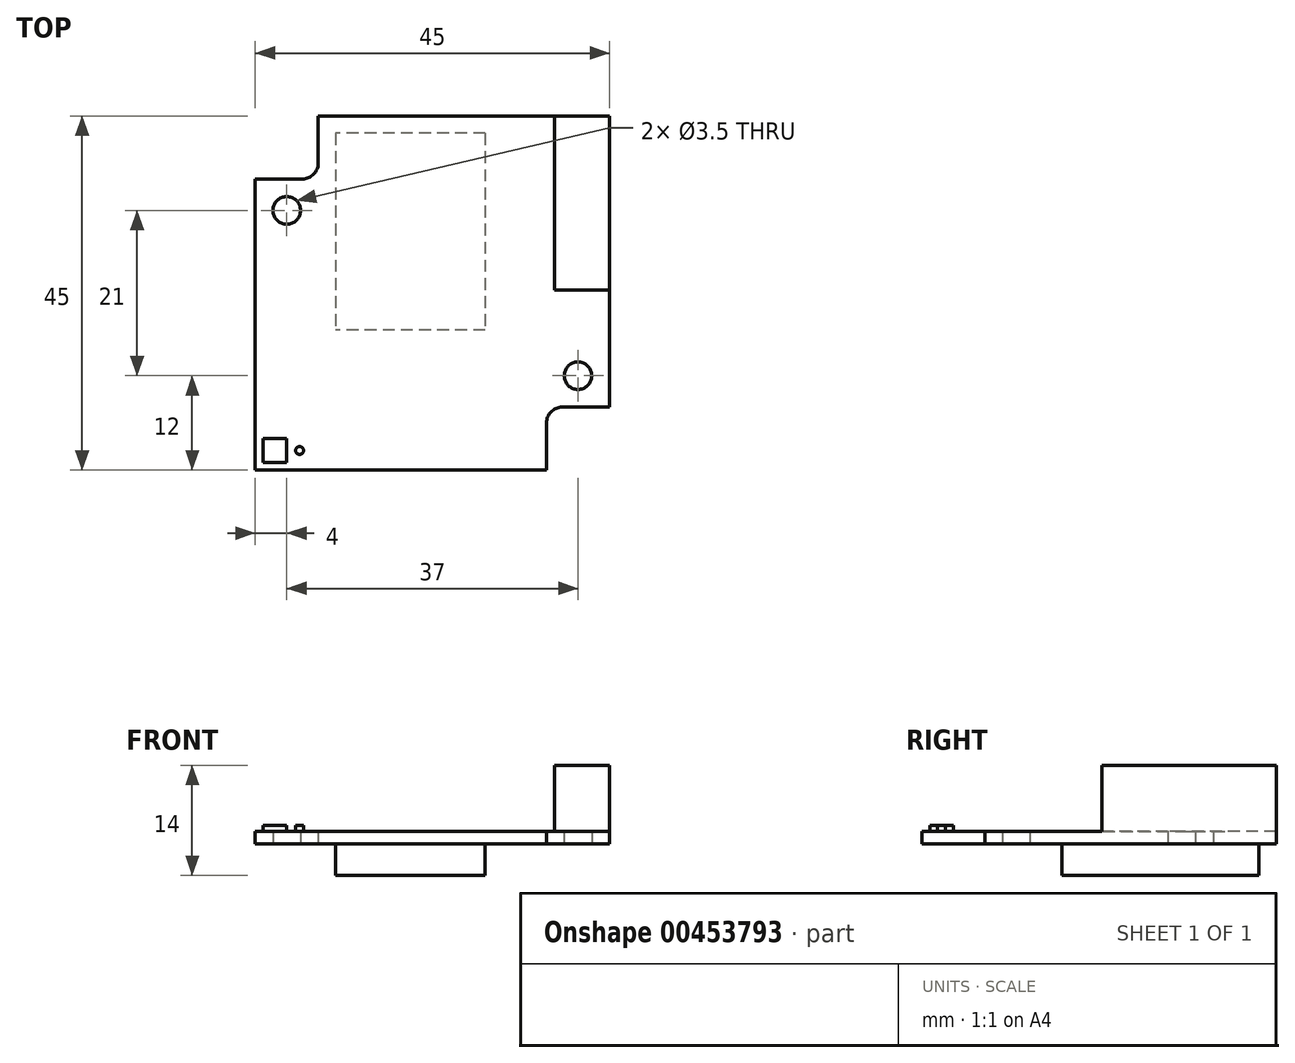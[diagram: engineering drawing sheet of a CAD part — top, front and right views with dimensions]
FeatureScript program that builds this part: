
annotation { "Feature Type Name" : "Feature", "Feature Type Description" : "" }
export const myFeature = defineFeature(function(context is Context, id is Id, definition is map)
    precondition{}
    {
        {
            var Q0;
            Q0=qCreatedBy(makeId("Top.planeOp"),FACE);
            var sketch = newSketch(context, id + "F0", { "sketchPlane" : qUnion([Q0])});
            skLineSegment(sketch, "E0.bottom", {"start": v(14.5, -22.5) * mm, "end": v(-22.5, -22.5) * mm});
            skLineSegment(sketch, "E0.top", {"start": v(22.5, 22.5) * mm, "end": v(-14.5, 22.5) * mm});
            skLineSegment(sketch, "E0.left", {"start": v(22.5, -14.5) * mm, "end": v(22.5, 22.5) * mm});
            skLineSegment(sketch, "E0.right", {"start": v(-22.5, -22.5) * mm, "end": v(-22.5, 14.5) * mm});
            skPoint(sketch, "E0.middle", {"position": v(0, 0) * mm});
            skLineSegment(sketch, "E1.top", {"start": v(-22.5, 14.5) * mm, "end": v(-16.5, 14.5) * mm});
            skLineSegment(sketch, "E1.right", {"start": v(-14.5, 22.5) * mm, "end": v(-14.5, 16.5) * mm});
            skLineSegment(sketch, "E2.top", {"start": v(22.5, -14.5) * mm, "end": v(16.5, -14.5) * mm});
            skLineSegment(sketch, "E2.right", {"start": v(14.5, -22.5) * mm, "end": v(14.5, -16.5) * mm});
            skPoint(sketch, "E3.orphan", {"position": v(-22.5, 22.5) * mm});
            skPoint(sketch, "E4.orphan", {"position": v(22.5, -22.5) * mm});
            skPoint(sketch, "E5.visualSharp", {"position": v(-14.5, 14.5) * mm});
            skArc(sketch, "E5.filletArc", {"start": v(-16.5, 14.5) * mm, "mid": v(-15.09, 15.09) * mm, "end": v(-14.5, 16.5) * mm});
            skPoint(sketch, "E6.visualSharp", {"position": v(14.5, -14.5) * mm});
            skArc(sketch, "E6.filletArc", {"start": v(16.5, -14.5) * mm, "mid": v(15.09, -15.09) * mm, "end": v(14.5, -16.5) * mm});
            skSolve(sketch);
        }
        {
            var Q0;
            Q0 = qSketchRegion(id + "F0", true);
            extrude(context, id + "F1", {"entities" : qUnion([Q0]), "depth" : 1.6 * mm});
        }
        {
            var Q0;
            Q0=makeQuery(id+"F1.opExtrude","CAP_FACE",FACE,{"disambiguationData":[OSD([sQuery(id+"F0.wireOp",EDGE,"E0.bottom"),sQuery(id+"F0.wireOp",EDGE,"E0.top"),sQuery(id+"F0.wireOp",EDGE,"E0.left"),sQuery(id+"F0.wireOp",EDGE,"E0.right"),sQuery(id+"F0.wireOp",EDGE,"E1.top"),sQuery(id+"F0.wireOp",EDGE,"E1.right"),sQuery(id+"F0.wireOp",EDGE,"E2.top"),sQuery(id+"F0.wireOp",EDGE,"E2.right"),sQuery(id+"F0.wireOp",EDGE,"E5.filletArc"),sQuery(id+"F0.wireOp",EDGE,"E6.filletArc")])],"isStart":false});
            var sketch = newSketch(context, id + "F2", { "sketchPlane" : qUnion([Q0])});
            skLineSegment(sketch, "E7.bottom", {"start": v(6.71, 20.3) * mm, "end": v(-12.29, 20.3) * mm});
            skLineSegment(sketch, "E7.top", {"start": v(6.71, -4.7) * mm, "end": v(-12.29, -4.7) * mm});
            skLineSegment(sketch, "E7.left", {"start": v(6.71, 20.3) * mm, "end": v(6.71, -4.7) * mm});
            skLineSegment(sketch, "E7.right", {"start": v(-12.29, 20.3) * mm, "end": v(-12.29, -4.7) * mm});
            skSolve(sketch);
        }
        {
            var Q0;
            Q0 = qSketchRegion(id + "F2", true);
            extrude(context, id + "F3", {"entities" : qUnion([Q0]), "operationType" : NewBodyOperationType.ADD, "depth" : -5.6 * mm});
        }
        {
            var Q0;
            Q0=makeQuery(id+"F1.opExtrude","CAP_FACE",FACE,{"disambiguationData":[OSD([sQuery(id+"F0.wireOp",EDGE,"E0.bottom"),sQuery(id+"F0.wireOp",EDGE,"E0.top"),sQuery(id+"F0.wireOp",EDGE,"E0.left"),sQuery(id+"F0.wireOp",EDGE,"E0.right"),sQuery(id+"F0.wireOp",EDGE,"E1.top"),sQuery(id+"F0.wireOp",EDGE,"E1.right"),sQuery(id+"F0.wireOp",EDGE,"E2.top"),sQuery(id+"F0.wireOp",EDGE,"E2.right"),sQuery(id+"F0.wireOp",EDGE,"E5.filletArc"),sQuery(id+"F0.wireOp",EDGE,"E6.filletArc")])],"isStart":false});
            var sketch = newSketch(context, id + "F4", { "sketchPlane" : qUnion([Q0])});
            skLineSegment(sketch, "E8.bottom", {"start": v(15.5, 22.5) * mm, "end": v(22.5, 22.5) * mm});
            skLineSegment(sketch, "E8.top", {"start": v(15.5, 0.4) * mm, "end": v(22.5, 0.4) * mm});
            skLineSegment(sketch, "E8.left", {"start": v(15.5, 22.5) * mm, "end": v(15.5, 0.4) * mm});
            skLineSegment(sketch, "E8.right", {"start": v(22.5, 22.5) * mm, "end": v(22.5, 0.4) * mm});
            skSolve(sketch);
        }
        {
            var Q0;
            Q0 = qSketchRegion(id + "F4", true);
            extrude(context, id + "F5", {"entities" : qUnion([Q0]), "operationType" : NewBodyOperationType.ADD, "depth" : 8.4 * mm});
        }
        {
            var Q0;
            Q0=makeQuery(id+"F1.opExtrude","CAP_FACE",FACE,{"disambiguationData":[OSD([sQuery(id+"F0.wireOp",EDGE,"E0.bottom"),sQuery(id+"F0.wireOp",EDGE,"E0.top"),sQuery(id+"F0.wireOp",EDGE,"E0.left"),sQuery(id+"F0.wireOp",EDGE,"E0.right"),sQuery(id+"F0.wireOp",EDGE,"E1.top"),sQuery(id+"F0.wireOp",EDGE,"E1.right"),sQuery(id+"F0.wireOp",EDGE,"E2.top"),sQuery(id+"F0.wireOp",EDGE,"E2.right"),sQuery(id+"F0.wireOp",EDGE,"E5.filletArc"),sQuery(id+"F0.wireOp",EDGE,"E6.filletArc")])],"isStart":false});
            var sketch = newSketch(context, id + "F6", { "sketchPlane" : qUnion([Q0])});
            skLineSegment(sketch, "E9.bottom", {"start": v(-21.5, -18.5) * mm, "end": v(-18.5, -18.5) * mm});
            skLineSegment(sketch, "E9.top", {"start": v(-21.5, -21.5) * mm, "end": v(-18.5, -21.5) * mm});
            skLineSegment(sketch, "E9.left", {"start": v(-21.5, -18.5) * mm, "end": v(-21.5, -21.5) * mm});
            skLineSegment(sketch, "E9.right", {"start": v(-18.5, -18.5) * mm, "end": v(-18.5, -21.5) * mm});
            skCircle(sketch, "E10", {"center": v(-16.87, -20) * mm, "radius": 0.5 * mm});
            skPoint(sketch, "E10.centerSnap0", {"position": v(-18.5, -20) * mm});
            skSolve(sketch);
        }
        {
            var Q0;
            Q0 = qSketchRegion(id + "F6", true);
            extrude(context, id + "F7", {"entities" : qUnion([Q0]), "operationType" : NewBodyOperationType.ADD, "depth" : 0.75 * mm});
        }
        {
            var Q0;
            Q0=makeQuery(id+"F1.opExtrude","CAP_FACE",FACE,{"disambiguationData":[OSD([sQuery(id+"F0.wireOp",EDGE,"E0.bottom"),sQuery(id+"F0.wireOp",EDGE,"E0.top"),sQuery(id+"F0.wireOp",EDGE,"E0.left"),sQuery(id+"F0.wireOp",EDGE,"E0.right"),sQuery(id+"F0.wireOp",EDGE,"E1.top"),sQuery(id+"F0.wireOp",EDGE,"E1.right"),sQuery(id+"F0.wireOp",EDGE,"E2.top"),sQuery(id+"F0.wireOp",EDGE,"E2.right"),sQuery(id+"F0.wireOp",EDGE,"E5.filletArc"),sQuery(id+"F0.wireOp",EDGE,"E6.filletArc")])],"isStart":true});
            var sketch = newSketch(context, id + "F8", { "sketchPlane" : qUnion([Q0])});
            skCircle(sketch, "E11", {"center": v(-18.5, -10.5) * mm, "radius": 1.75 * mm});
            skCircle(sketch, "E12", {"center": v(18.5, 10.5) * mm, "radius": 1.75 * mm});
            skSolve(sketch);
        }
        {
            var Q0;
            Q0 = qSketchRegion(id + "F8", true);
            extrude(context, id + "F9", {"entities" : qUnion([Q0]), "operationType" : NewBodyOperationType.REMOVE, "oppositeDirection" : true, "depth" : 2 * mm});
        }
    });
